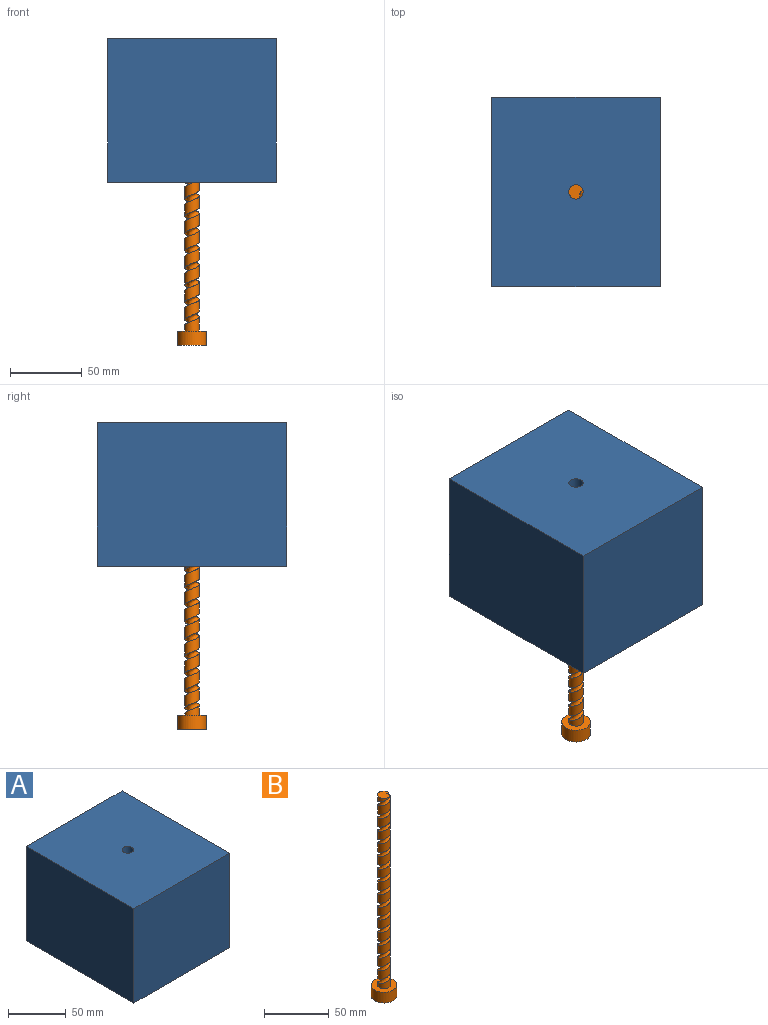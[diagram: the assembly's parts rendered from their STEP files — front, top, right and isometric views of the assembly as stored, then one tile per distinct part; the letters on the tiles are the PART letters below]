
ASSEMBLY  parts=2 mates=1
PART A: 7 faces, bbox 117.3x131.8x100 mm
  f0: plane 117.3x100mm, normal (0,-1,0), area 11729.5mm2, adj f1,f3,f4,f5
  f1: plane 131.81x100mm, normal (1,0,0), area 13181.1mm2, adj f0,f2,f4,f5
  f2: plane 117.3x100mm, normal (0,1,0), area 11729.5mm2, adj f1,f3,f4,f5
  f3: plane 131.81x100mm, normal (-1,0,0), area 13181.1mm2, adj f0,f2,f4,f5
  f4: plane 131.81x117.3mm, normal (0,0,1), area 15382.2mm2, adj f0,f1,f2,f3,f6
  f5: plane 131.81x117.3mm, normal (0,0,-1), area 15382.2mm2, adj f0,f1,f2,f3,f6
  f6: cylinder r=5mm len=100mm, axis (0,0,1), area 3141.6mm2, adj f4,f5
PART B: 8 faces, bbox 20x20x192 mm
  f0: plane 10x10mm, normal (0,0,1), area 71.7mm2, adj f4,f5,f7
  f1: cylinder r=10mm len=20mm, axis (0,0,-1), area 628.3mm2, adj f2,f3
  f2: plane 20x20mm, normal (0,0,1), area 226mm2, adj f1,f4,f6,f7
  f3: plane 20x20mm, normal (0,0,-1), area 314.2mm2, adj f1
  f4: cylinder r=5mm len=180mm, axis (0,0,-1), area 3779.3mm2, adj f0,f2,f5,f6,f7
  f5: plane 2x2mm, normal (0,-1,0), area 3.1mm2, adj f0,f4,f7
  f6: plane 4x4mm, normal (0,1,0), area 9.4mm2, adj f2,f4,f7
  f7: bspline ~184x13.99mm, area 2346.2mm2, adj f0,f2,f4,f5,f6
PLACE A t=(76.8,22.33,150.48)mm
PLACE B t=(76.8,22.33,36.81)mm
MATE cylindrical B.f4 <-> A.f6  axis (0,0,1) through (76.8,22.33,226.81)mm
